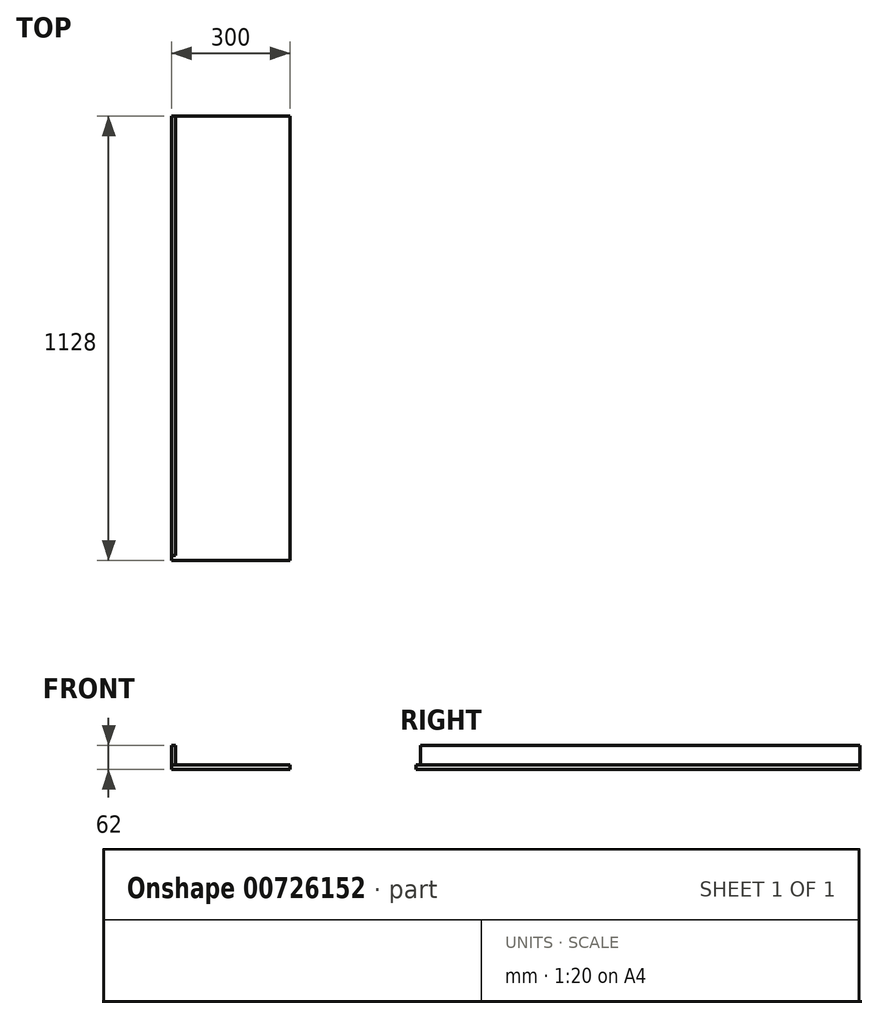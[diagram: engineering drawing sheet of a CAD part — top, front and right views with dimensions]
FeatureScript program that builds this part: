
annotation { "Feature Type Name" : "Feature", "Feature Type Description" : "" }
export const myFeature = defineFeature(function(context is Context, id is Id, definition is map)
    precondition{}
    {
        {
            var Q0;
            Q0=qCreatedBy(makeId("Top.planeOp"),FACE);
            var sketch = newSketch(context, id + "F0", { "sketchPlane" : qUnion([Q0])});
            skLineSegment(sketch, "E0.bottom", {"start": v(-150, 564) * mm, "end": v(150, 564) * mm});
            skLineSegment(sketch, "E0.top", {"start": v(-150, -564) * mm, "end": v(150, -564) * mm});
            skLineSegment(sketch, "E0.left", {"start": v(-150, 564) * mm, "end": v(-150, -564) * mm});
            skLineSegment(sketch, "E0.right", {"start": v(150, 564) * mm, "end": v(150, -564) * mm});
            skLineSegment(sketch, "E1", {"start": v(0, -564) * mm, "end": v(0, 564) * mm, "construction": true});
            skSolve(sketch);
        }
        {
            var Q0;
            Q0 = qSketchRegion(id + "F0", true);
            extrude(context, id + "F1", {"entities" : qUnion([Q0]), "depth" : 12 * mm, "offsetDistance" : 25 * mm});
        }
        {
            var Q0;
            Q0=makeQuery(id+"F1.opExtrude","CAP_FACE",FACE,{"disambiguationData":[OSD([sQuery(id+"F0.wireOp",EDGE,"E0.bottom"),sQuery(id+"F0.wireOp",EDGE,"E0.top"),sQuery(id+"F0.wireOp",EDGE,"E0.left"),sQuery(id+"F0.wireOp",EDGE,"E0.right")])],"isStart":false});
            var sketch = newSketch(context, id + "F2", { "sketchPlane" : qUnion([Q0])});
            skLineSegment(sketch, "E2.bottom", {"start": v(-150, 564) * mm, "end": v(-140, 564) * mm});
            skLineSegment(sketch, "E2.top", {"start": v(-150, -552) * mm, "end": v(-140, -552) * mm});
            skLineSegment(sketch, "E2.left", {"start": v(-150, 564) * mm, "end": v(-150, -552) * mm});
            skLineSegment(sketch, "E2.right", {"start": v(-140, 564) * mm, "end": v(-140, -552) * mm});
            skSolve(sketch);
        }
        {
            var Q0;
            Q0 = qSketchRegion(id + "F2", true);
            extrude(context, id + "F3", {"entities" : qUnion([Q0]), "operationType" : NewBodyOperationType.ADD, "depth" : 50 * mm, "offsetDistance" : 25 * mm});
        }
    });
